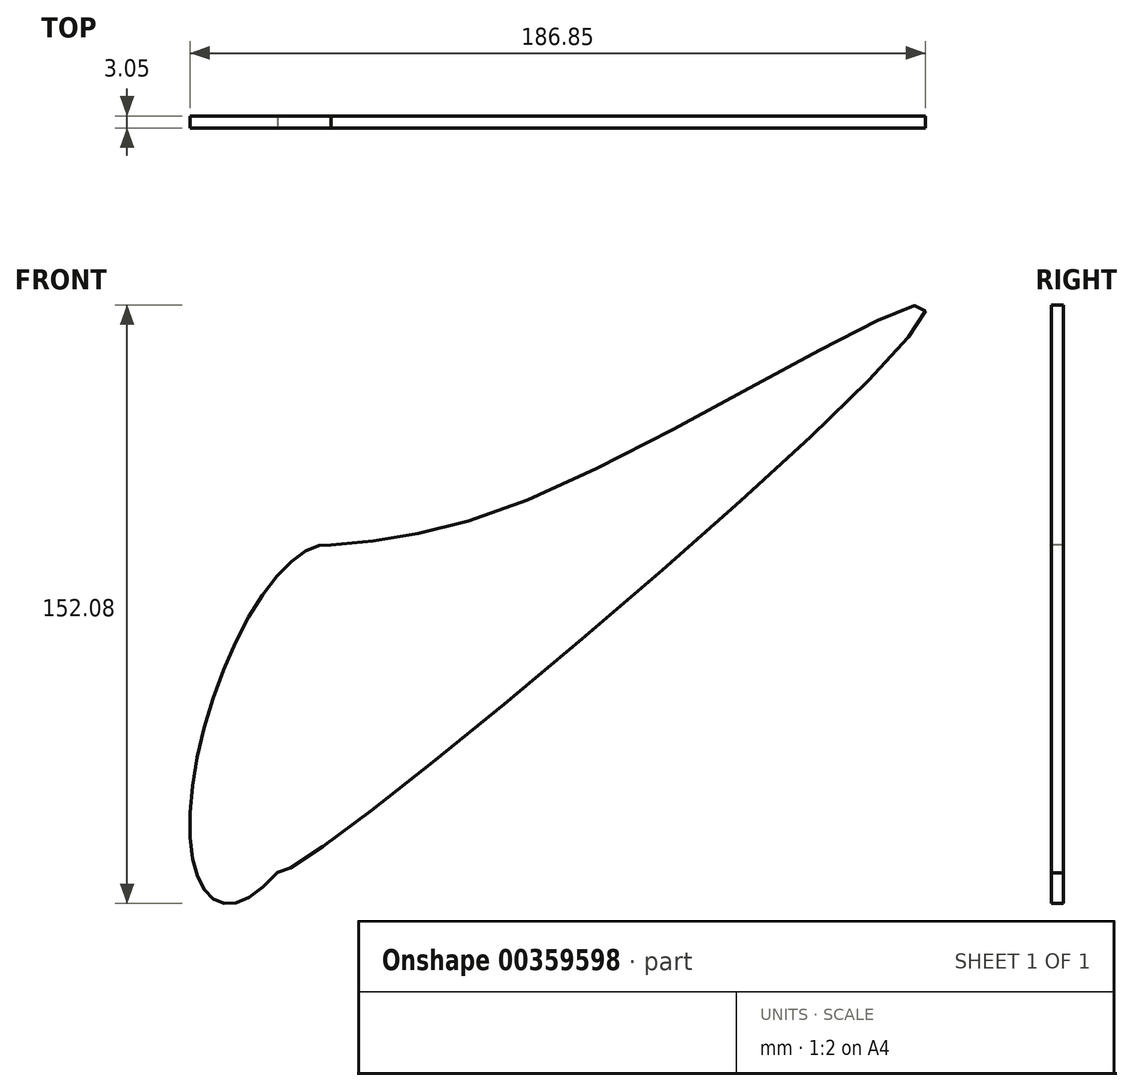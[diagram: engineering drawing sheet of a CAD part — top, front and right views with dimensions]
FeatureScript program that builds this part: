
annotation { "Feature Type Name" : "Feature", "Feature Type Description" : "" }
export const myFeature = defineFeature(function(context is Context, id is Id, definition is map)
    precondition{}
    {
        {
            var Q0;
            Q0=qCreatedBy(makeId("Front.planeOp"),FACE);
            var sketch = newSketch(context, id + "F0", { "sketchPlane" : qUnion([Q0])});
            skEllipse(sketch, "E0", {"center": v(0, 0) * mm, "majorRadius": 47.6 * mm, "minorRadius": 17.64 * mm, "majorAxis": v(0.3, 0.95)});
            skPoint(sketch, "E1.0.internal.snap0", {"position": v(14.62, 45.3) * mm});
            skPoint(sketch, "E1.7.internal.snap0", {"position": v(16.79, -5.42) * mm});
            skFitSpline(sketch, "E1", {"points": [v(10.25, 45.3) * mm, v(69.79, 59.65) * mm, v(164.17, 106.26) * mm, v(68.46, 14.08) * mm, v(0, -37.72) * mm, v(10.24, -21.7) * mm, v(21.94, 18.85) * mm, v(16.79, 44.13) * mm], "startDerivative": vector(341.85, 25.42) * mm, "endDerivative": vector(-83.53, 251.37) * mm});
            skSolve(sketch);
        }
        {
            var Q0;
            {var subQ0=sQuery(id+"F0.wireOp",EDGE,"E1");var subQ1=sQuery(id+"F0.wireOp",EDGE,"E0");var subQ5=makeQuery(id+"F0.imprint","INTERSECT",VERTEX,{"disambiguationData":[OD(3.0)],"derivedFrom":[subQ1,subQ0]});Q0=makeQuery(id+"F0.imprint","IMPRINT",FACE,{"disambiguationData":[TD([[makeQuery(id+"F0.imprint","IMPRINT",EDGE,{"disambiguationData":[TD([[subQ5,-1.0]])],"derivedFrom":subQ1}),-1.0]])]});}
            var sketch = newSketch(context, id + "F1", { "sketchPlane" : qUnion([Q0])});
            skSolve(sketch);
        }
        {
            var Q0;
            {var subQ0=sQuery(id+"F0.wireOp",EDGE,"E1");var subQ1=sQuery(id+"F0.wireOp",EDGE,"E0");var subQ2=makeQuery(id+"F0.imprint","INTERSECT",VERTEX,{"disambiguationData":[OD(4.0)],"derivedFrom":[subQ1,subQ0]});Q0=makeQuery(id+"F0.imprint","IMPRINT",FACE,{"disambiguationData":[TD([[makeQuery(id+"F0.imprint","IMPRINT",EDGE,{"disambiguationData":[TD([[subQ2,-1.0]])],"derivedFrom":subQ1}),-1.0]])]});}
            var Q1;
            {var subQ0=sQuery(id+"F0.wireOp",EDGE,"E1");var subQ1=sQuery(id+"F0.wireOp",EDGE,"E0");var subQ5=makeQuery(id+"F0.imprint","INTERSECT",VERTEX,{"disambiguationData":[OD(3.0)],"derivedFrom":[subQ1,subQ0]});Q1=makeQuery(id+"F0.imprint","IMPRINT",FACE,{"disambiguationData":[TD([[makeQuery(id+"F0.imprint","IMPRINT",EDGE,{"disambiguationData":[TD([[subQ5,-1.0]])],"derivedFrom":subQ1}),-1.0]])]});}
            var Q2;
            {var subQ0=sQuery(id+"F0.wireOp",EDGE,"E1");var subQ1=sQuery(id+"F0.wireOp",EDGE,"E0");var subQ6=makeQuery(id+"F0.imprint","INTERSECT",VERTEX,{"disambiguationData":[OD(0.0)],"derivedFrom":[subQ1,subQ0]});Q2=makeQuery(id+"F0.imprint","IMPRINT",FACE,{"disambiguationData":[TD([[makeQuery(id+"F0.imprint","IMPRINT",EDGE,{"disambiguationData":[TD([[subQ6,-1.0]])],"derivedFrom":subQ1}),1.0]])]});}
            var Q3;
            {var subQ0=sQuery(id+"F0.wireOp",EDGE,"E1");var subQ1=sQuery(id+"F0.wireOp",EDGE,"E0");var subQ2=makeQuery(id+"F0.imprint","INTERSECT",VERTEX,{"disambiguationData":[OD(3.0)],"derivedFrom":[subQ1,subQ0]});Q3=makeQuery(id+"F0.imprint","IMPRINT",FACE,{"disambiguationData":[TD([[makeQuery(id+"F0.imprint","IMPRINT",EDGE,{"disambiguationData":[TD([[subQ2,-1.0]])],"derivedFrom":subQ1}),1.0]])]});}
            var Q4;
            {var subQ0=sQuery(id+"F0.wireOp",EDGE,"E1");var subQ1=sQuery(id+"F0.wireOp",EDGE,"E0");var subQ2=makeQuery(id+"F0.imprint","INTERSECT",VERTEX,{"disambiguationData":[OD(1.0)],"derivedFrom":[subQ1,subQ0]});Q4=makeQuery(id+"F0.imprint","IMPRINT",FACE,{"disambiguationData":[TD([[makeQuery(id+"F0.imprint","IMPRINT",EDGE,{"disambiguationData":[TD([[subQ2,1.0]])],"derivedFrom":subQ1}),1.0]])]});}
            var Q5;
            {var subQ0=sQuery(id+"F0.wireOp",EDGE,"E1");var subQ1=sQuery(id+"F0.wireOp",EDGE,"E0");var subQ3=makeQuery(id+"F0.imprint","INTERSECT",VERTEX,{"disambiguationData":[OD(3.0)],"derivedFrom":[subQ1,subQ0]});Q5=makeQuery(id+"F1.imprint","IMPRINT",FACE,{"disambiguationData":[TD([[makeQuery(id+"F1.imprint","IMPRINT",EDGE,{"derivedFrom":makeQuery(id+"F0.imprint","IMPRINT",EDGE,{"disambiguationData":[TD([[subQ3,-1.0]])],"derivedFrom":subQ1})}),-1.0]])]});}
            var Q6;
            {var subQ0=sQuery(id+"F0.wireOp",EDGE,"E1");var subQ1=sQuery(id+"F0.wireOp",EDGE,"E0");var subQ2=makeQuery(id+"F0.imprint","INTERSECT",VERTEX,{"disambiguationData":[OD(0.0)],"derivedFrom":[subQ1,subQ0]});Q6=makeQuery(id+"F0.imprint","IMPRINT",FACE,{"disambiguationData":[TD([[makeQuery(id+"F0.imprint","IMPRINT",EDGE,{"disambiguationData":[TD([[subQ2,1.0]])],"derivedFrom":subQ1}),1.0]])]});}
            extrude(context, id + "F2", {"entities" : qUnion([Q0, Q1, Q2, Q3, Q4, Q5, Q6]), "oppositeDirection" : true, "depth" : 3.05 * mm});
        }
    });
